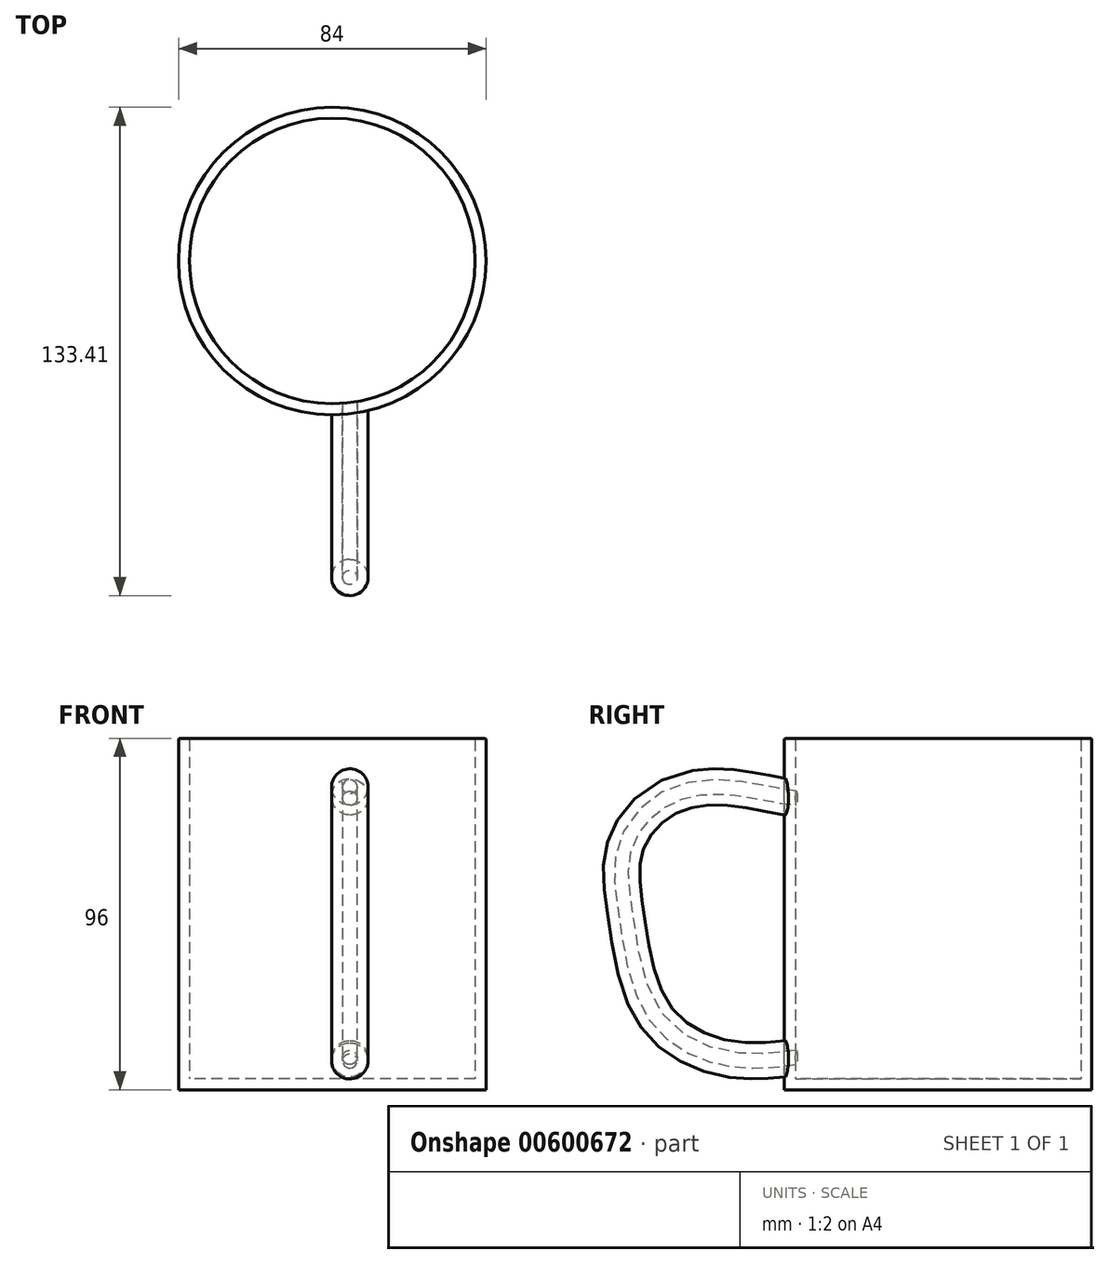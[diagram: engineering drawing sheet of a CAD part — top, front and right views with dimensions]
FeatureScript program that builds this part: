
annotation { "Feature Type Name" : "Feature", "Feature Type Description" : "" }
export const myFeature = defineFeature(function(context is Context, id is Id, definition is map)
    precondition{}
    {
        {
            var Q0;
            Q0=qCreatedBy(makeId("Top.planeOp"),FACE);
            var sketch = newSketch(context, id + "F0", { "sketchPlane" : qUnion([Q0])});
            skCircle(sketch, "E0", {"center": v(-4.8, 0) * mm, "radius": 42 * mm});
            skSolve(sketch);
        }
        {
            var Q0;
            Q0 = qSketchRegion(id + "F0", true);
            extrude(context, id + "F1", {"entities" : qUnion([Q0]), "endBound" : BoundingType.SYMMETRIC, "depth" : 96 * mm, "offsetDistance" : 25 * mm});
        }
        {
            var Q0;
            Q0=qCreatedBy(makeId("Right.planeOp"),FACE);
            var sketch = newSketch(context, id + "F2", { "sketchPlane" : qUnion([Q0])});
            skFitSpline(sketch, "E1", {"points": [v(-34.8, 27.75) * mm, v(-55.53, 30.86) * mm, v(-72.23, 28.72) * mm, v(-82.04, 17.39) * mm, v(-81.66, 0) * mm, v(-74.01, -26.25) * mm, v(-53.7, -36.4) * mm, v(-34.87, -35.19) * mm], "startDerivative": vector(-157.66, 6.37) * mm, "endDerivative": vector(105.82, 6.82) * mm});
            skSolve(sketch);
        }
        {
            var Q0;
            Q0=qCreatedBy(makeId("Front.planeOp"),FACE);
            cPlane(context, id + "F3", {"entities" : qUnion([Q0]), "cplaneType" : CPlaneType.OFFSET, "offset" : 42 * mm, "width" : 150 * mm, "height" : 150 * mm});
        }
        {
            var Q0;
            Q0=qCreatedBy(id+"F3.planeOp",FACE);
            var sketch = newSketch(context, id + "F4", { "sketchPlane" : qUnion([Q0])});
            skCircle(sketch, "E2", {"center": v(0, 32.1) * mm, "radius": 5 * mm});
            skSolve(sketch);
        }
        {
            var Q0;
            Q0=makeQuery(id+"F4.imprint","IMPRINT",FACE,{"disambiguationData":[TD([[makeQuery(id+"F4.imprint","IMPRINT",EDGE,{"derivedFrom":sQuery(id+"F4.wireOp",EDGE,"E2")}),1.0]])]});
            var Q1;
            Q1=sQuery(id+"F2.wireOp",EDGE,"E1");
            sweep(context, id + "F5", {"operationType" : NewBodyOperationType.ADD, "profiles" : qUnion([Q0]), "path" : qUnion([Q1])});
        }
        {
            var Q0;
            Q0=makeQuery(id+"F1.opExtrude","CAP_FACE",FACE,{"disambiguationData":[OSD([sQuery(id+"F0.wireOp",EDGE,"E0")])],"isStart":false});
            shell(context, id + "F6", {"entities" : qUnion([Q0]), "thickness" : 3 * mm});
        }
        {
            var Q0;
            Q0=makeQuery(id+"F1.opExtrude","CAP_EDGE",EDGE,{"disambiguationData":[OSD([sQuery(id+"F0.wireOp",EDGE,"E0")])],"isStart":false});
            var Q1;
            {var subQ0=sQuery(id+"F0.wireOp",EDGE,"E0");Q1=makeQuery(id+"F6.opShell","OFFSET_EDGE",EDGE,{"disambiguationData":[OSD([subQ0]),TDD([makeQuery(id+"F1.opExtrude","CAP_EDGE",EDGE,{"disambiguationData":[OSD([subQ0])],"isStart":false})])]});}
            fillet(context, id + "F7", {"entities" : qUnion([Q0, Q1]), "radius" : 0.5 * mm, "tangentPropagation" : true, "allowEdgeOverflow" : false});
        }
    });
